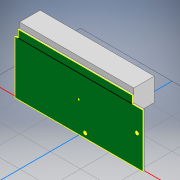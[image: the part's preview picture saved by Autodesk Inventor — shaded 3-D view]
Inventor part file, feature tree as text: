
AUTODESK INVENTOR PART (.ipt)
format: ipt  version: 2022 (Build 260153000, 153)  size: 152,064 bytes
history: native  units: mm
features: sketch x4, extrude x3, other x1, projected_geometry x1
ambient origin geometry x8: Origin, YZ Plane, XZ Plane, XY Plane, X Axis, Y Axis, Z Axis, Center Point
bodies: Body1 (feature_tree)
feature tree (9):
  other  "Твердое тело1"
  extrude  "Выдавливание1"  Depth=84.0mm
  extrude  "Выдавливание2"  Depth=40.0mm
  extrude  "Выдавливание3"  Depth=5.0mm
  sketch  "Эскиз4"
  sketch  "Эскиз1"
  sketch  "Эскиз2"
  sketch  "Эскиз3"
  projected_geometry  "Спроецированная петля1"
